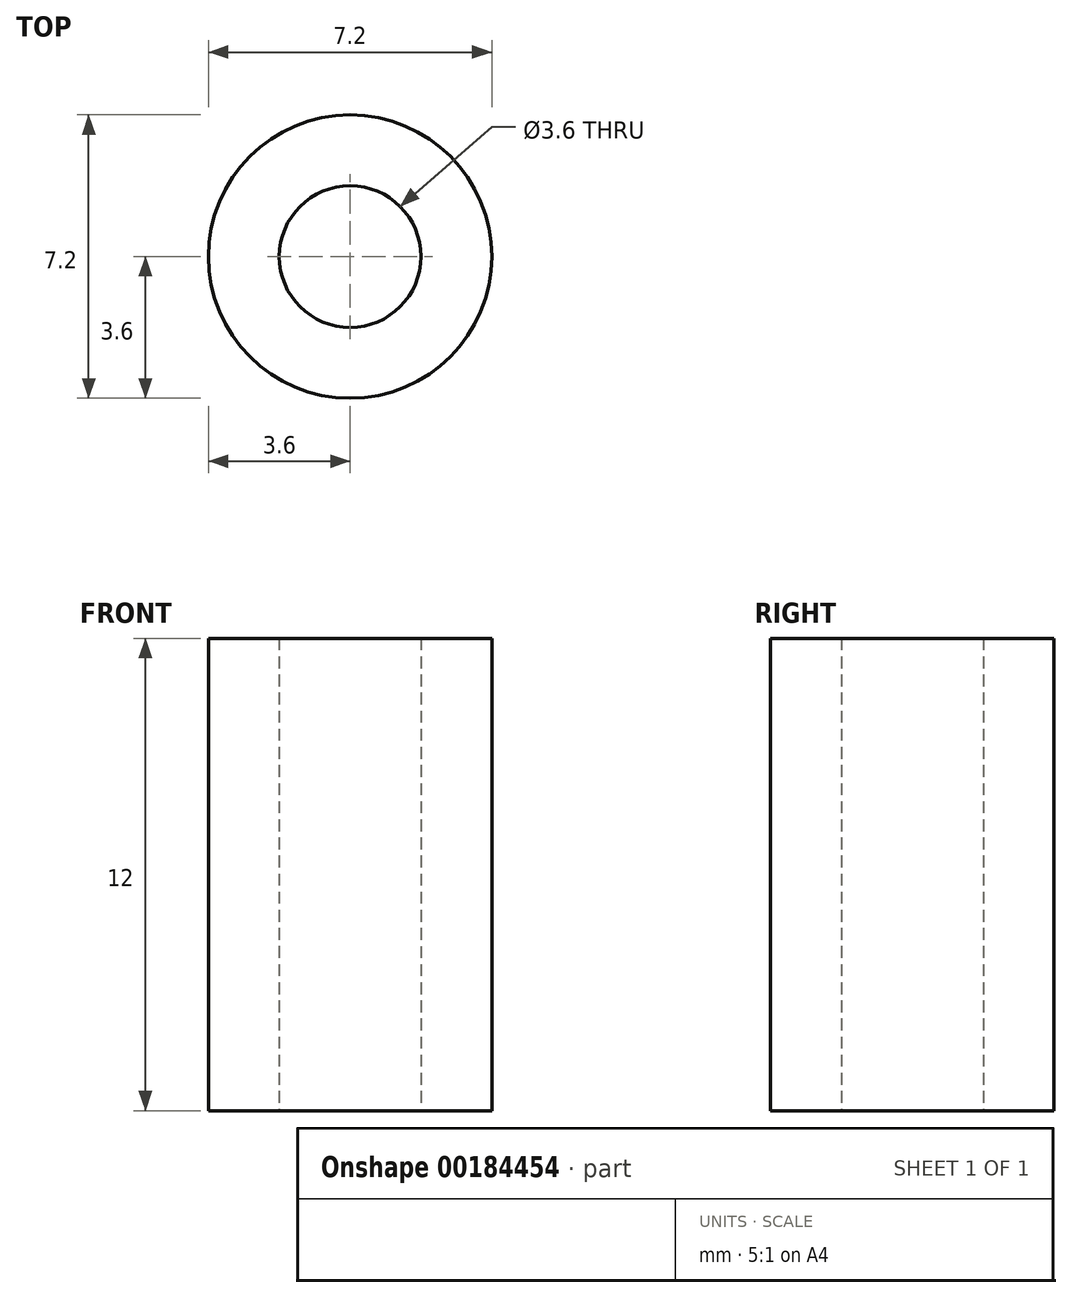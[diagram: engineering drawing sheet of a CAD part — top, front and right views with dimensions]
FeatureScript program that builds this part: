
annotation { "Feature Type Name" : "Feature", "Feature Type Description" : "" }
export const myFeature = defineFeature(function(context is Context, id is Id, definition is map)
    precondition{}
    {
        {
            var Q0;
            Q0=qCreatedBy(makeId("Top.planeOp"),FACE);
            var sketch = newSketch(context, id + "F0", { "sketchPlane" : qUnion([Q0])});
            skCircle(sketch, "E0", {"center": v(0, 0) * mm, "radius": 3.6 * mm});
            skCircle(sketch, "E1", {"center": v(0, 0) * mm, "radius": 1.8 * mm});
            skSolve(sketch);
        }
        {
            var Q0;
            Q0=makeQuery(id+"F0.imprint","IMPRINT",FACE,{"disambiguationData":[TD([[makeQuery(id+"F0.imprint","IMPRINT",EDGE,{"derivedFrom":sQuery(id+"F0.wireOp",EDGE,"E0")}),1.0]])]});
            extrude(context, id + "F1", {"entities" : qUnion([Q0]), "depth" : 12 * mm});
        }
    });
